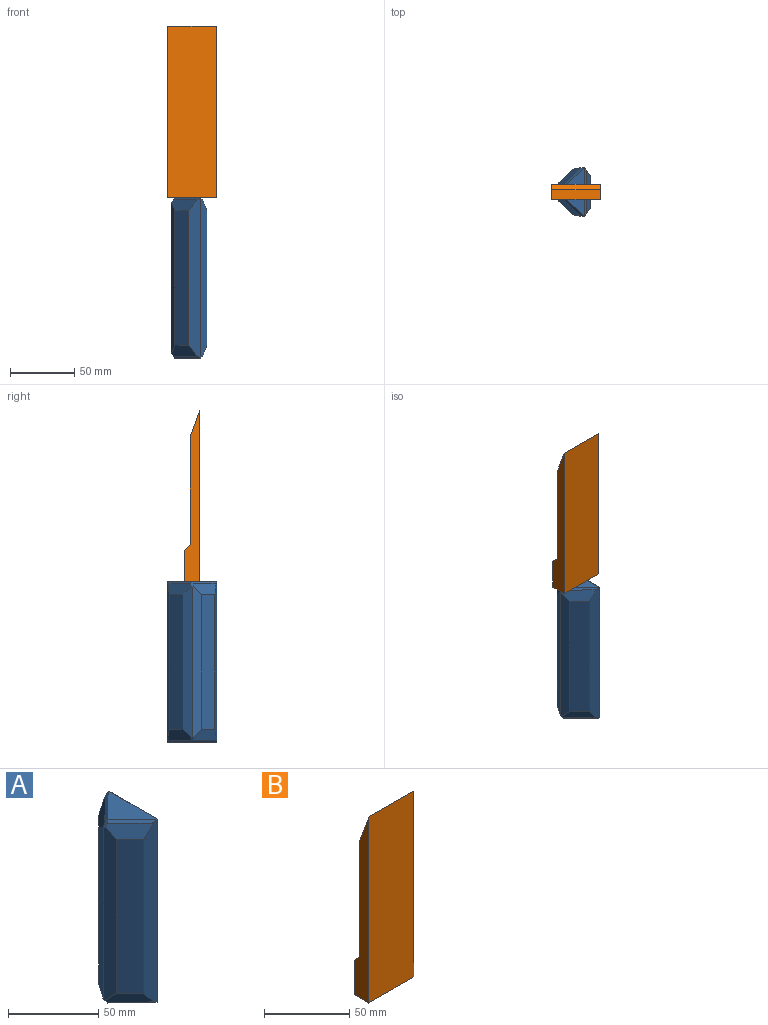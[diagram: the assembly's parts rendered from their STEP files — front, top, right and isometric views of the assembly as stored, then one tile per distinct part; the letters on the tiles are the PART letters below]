
ASSEMBLY  parts=2 mates=1
PART A: 25 faces, bbox 27.9x38.5x124.4 mm
  f0: plane 38.46x20.2mm, normal (0,0,-1), area 394.7mm2, adj f5,f6,f7,f19,f21,f22,f23
  f1: plane 38.46x20.2mm, normal (0,0,1), area 394.7mm2, adj f9,f10,f12,f19,f21,f22,f23
  f2: plane 104.65x10.87mm, normal (-0.7,0.72,0), area 1586mm2, adj f13,f15,f16,f19
  f3: plane 104.65x10.83mm, normal (-0.69,-0.72,0), area 1573.4mm2, adj f14,f17,f18,f21
  f4: plane 104.65x23.22mm, normal (1,0,0), area 2429.5mm2, adj f20,f22,f23,f24
  f5: plane 20.8x19.27mm, normal (-0.49,0.51,-0.71), area 52.8mm2, adj f0,f8,f16,f19
  f6: plane 38.06x1.4mm, normal (0.71,0,-0.71), area 71.4mm2, adj f0,f20,f22,f23
  f7: plane 20.82x19.1mm, normal (-0.49,-0.51,-0.71), area 52.6mm2, adj f0,f8,f17,f21
  f8: plane 3.97x2.76mm, normal (-0.82,0,-0.57), area 6.8mm2, adj f5,f7,f13,f14,f16,f17
  f9: plane 20.8x19.27mm, normal (-0.49,0.51,0.71), area 52.8mm2, adj f1,f11,f15,f19
  f10: plane 38.06x1.4mm, normal (0.71,0,0.71), area 71.4mm2, adj f1,f22,f23,f24
  f11: plane 3.97x2.76mm, normal (-0.82,0,0.57), area 6.8mm2, adj f9,f12,f13,f14,f15,f18
  f12: plane 20.82x19.1mm, normal (-0.49,-0.51,0.71), area 52.6mm2, adj f1,f11,f18,f21
  f13: plane 117.45x7.07mm, normal (-0.92,0.39,0), area 857.2mm2, adj f2,f8,f11,f14,f15,f16
  f14: plane 117.45x7.06mm, normal (-0.92,-0.39,0), area 857.2mm2, adj f3,f8,f11,f13,f17,f18
  f15: plane 19.74x18mm, normal (-0.64,0.66,0.38), area 197.6mm2, adj f2,f9,f11,f13,f19
  f16: plane 19.74x18mm, normal (-0.64,0.66,-0.38), area 197.6mm2, adj f2,f5,f8,f13,f19
  f17: plane 19.76x17.82mm, normal (-0.64,-0.67,-0.38), area 196.5mm2, adj f3,f7,f8,f14,f21
  f18: plane 19.76x17.82mm, normal (-0.64,-0.67,0.38), area 196.5mm2, adj f3,f11,f12,f14,f21
  f19: plane 124.4x8.98mm, normal (-0.18,0.98,0), area 1061.9mm2, adj f0,f1,f2,f5,f9,f15,f16,f22
  f20: plane 33.81x8.47mm, normal (0.92,0,-0.38), area 261.5mm2, adj f4,f6,f22,f23
  f21: plane 124.4x8.99mm, normal (-0.18,-0.98,0), area 1061.5mm2, adj f0,f1,f3,f7,f12,f17,f18,f23
  f22: plane 124.4x7.62mm, normal (0.83,0.55,0), area 1061.9mm2, adj f0,f1,f4,f6,f10,f19,f20,f24
  f23: plane 124.4x7.62mm, normal (0.83,-0.55,0), area 1061.5mm2, adj f0,f1,f4,f6,f10,f20,f21,f24
  f24: plane 33.81x8.47mm, normal (0.92,0,0.38), area 261.5mm2, adj f4,f10,f22,f23
PART B: 8 faces, bbox 37.4x12.1x133.6 mm
  f0: plane 133.58x37.38mm, normal (0,-1,0), area 4993.1mm2, adj f2,f3,f4,f7
  f1: plane 37.38x24.64mm, normal (0,1,0), area 921mm2, adj f2,f3,f4,f5
  f2: plane 37.38x12.14mm, normal (0,0,-1), area 453.8mm2, adj f0,f1,f3,f4
  f3: plane 133.58x12.14mm, normal (-1,0,0), area 1046.6mm2, adj f0,f1,f2,f5,f6,f7
  f4: plane 133.58x12.14mm, normal (1,0,0), area 1046.6mm2, adj f0,f1,f2,f5,f6,f7
  f5: plane 37.38x4.66mm, normal (0,0.71,0.71), area 246.5mm2, adj f1,f3,f4,f6
  f6: plane 83.44x37.38mm, normal (0,1,0), area 3118.7mm2, adj f3,f4,f5,f7
  f7: plane 37.38x20.84mm, normal (0,0.94,0.34), area 827.7mm2, adj f0,f3,f4,f6
PLACE A t=(-43.06,9.68,-148.7)mm
PLACE B at identity
MATE fastened A.f1 <-> B.f2  axis (0,0,1) through (-18.69,6.07,-24.3)mm
